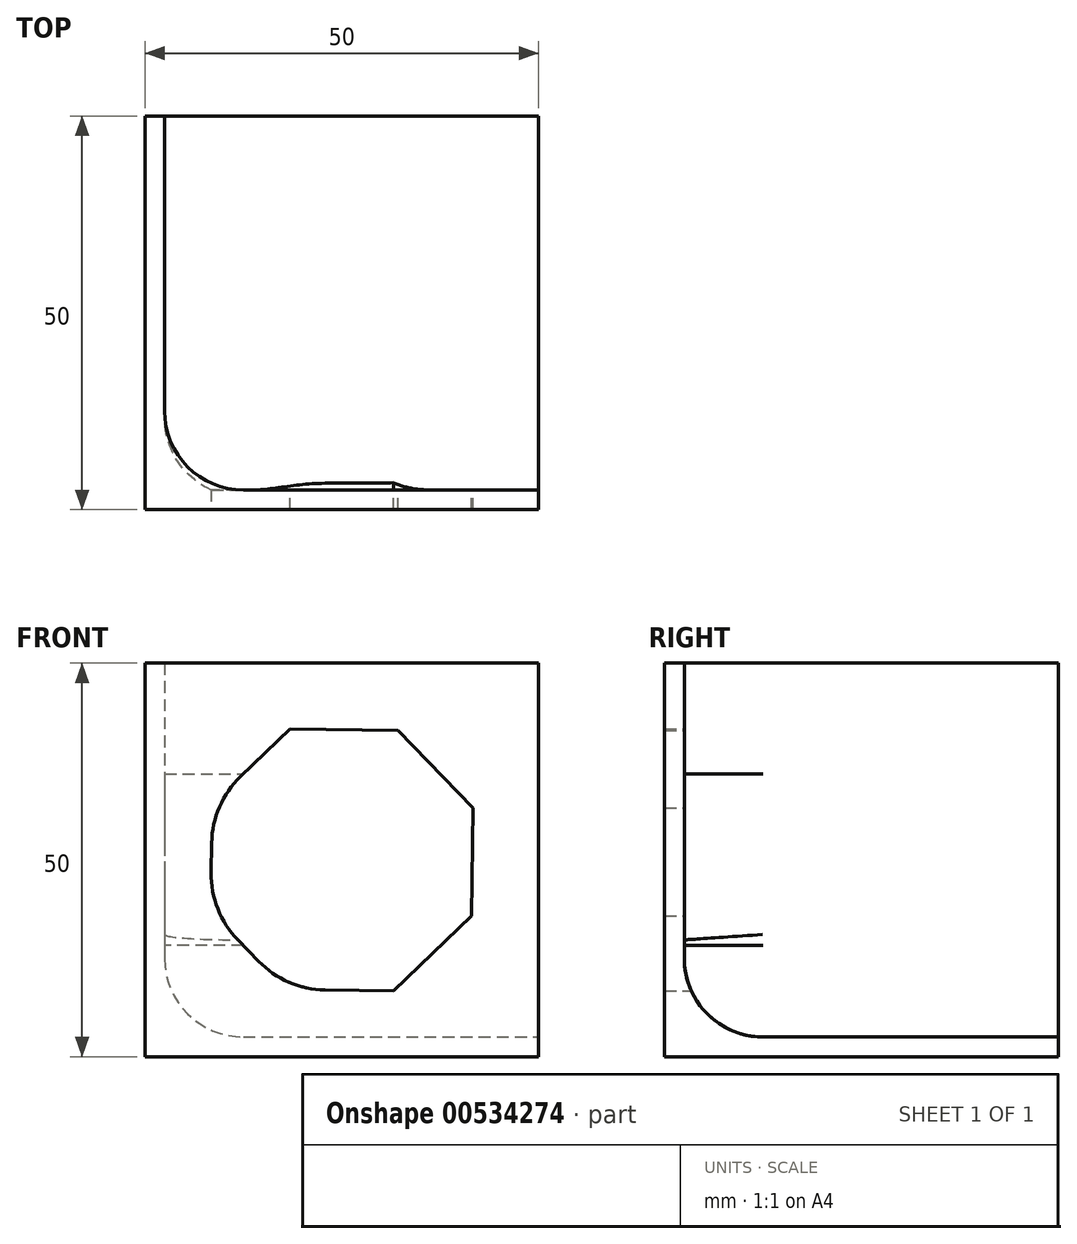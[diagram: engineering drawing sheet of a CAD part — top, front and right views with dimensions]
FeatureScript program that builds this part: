
annotation { "Feature Type Name" : "Feature", "Feature Type Description" : "" }
export const myFeature = defineFeature(function(context is Context, id is Id, definition is map)
    precondition{}
    {
        {
            var Q0;
            Q0=qCreatedBy(makeId("Top.planeOp"),FACE);
            var sketch = newSketch(context, id + "F0", { "sketchPlane" : qUnion([Q0])});
            skLineSegment(sketch, "E0.bottom", {"start": v(-25, -25) * mm, "end": v(25, -25) * mm});
            skLineSegment(sketch, "E0.top", {"start": v(-25, 25) * mm, "end": v(25, 25) * mm});
            skLineSegment(sketch, "E0.left", {"start": v(-25, -25) * mm, "end": v(-25, 25) * mm});
            skLineSegment(sketch, "E0.right", {"start": v(25, -25) * mm, "end": v(25, 25) * mm});
            skLineSegment(sketch, "E1", {"start": v(0, 0) * mm, "end": v(0, 66.24) * mm, "construction": true});
            skSolve(sketch);
        }
        {
            var Q0;
            Q0=makeQuery(id+"F0.imprint","IMPRINT",FACE,{"disambiguationData":[TD([[makeQuery(id+"F0.imprint","IMPRINT",EDGE,{"derivedFrom":sQuery(id+"F0.wireOp",EDGE,"E0.bottom")}),1.0]])]});
            extrude(context, id + "F1", {"entities" : qUnion([Q0]), "depth" : 50 * mm, "offsetDistance" : 25 * mm, "symmetric" : true});
        }
        {
            var Q0;
            Q0=makeQuery(id+"F1.opExtrude","CAP_FACE",FACE,{"disambiguationData":[OSD([sQuery(id+"F0.wireOp",EDGE,"E0.bottom"),sQuery(id+"F0.wireOp",EDGE,"E0.top"),sQuery(id+"F0.wireOp",EDGE,"E0.left"),sQuery(id+"F0.wireOp",EDGE,"E0.right")])],"isStart":false});
            var Q1;
            Q1=makeQuery(id+"F1.opExtrude","SWEPT_FACE",FACE,{"disambiguationData":[OSD([sQuery(id+"F0.wireOp",EDGE,"E0.top")])]});
            var Q2;
            Q2=makeQuery(id+"F1.opExtrude","SWEPT_FACE",FACE,{"disambiguationData":[OSD([sQuery(id+"F0.wireOp",EDGE,"E0.right")])]});
            shell(context, id + "F2", {"entities" : qUnion([Q0, Q1, Q2]), "thickness" : 2.5 * mm});
        }
        {
            var Q0;
            Q0=qCreatedBy(makeId("Front.planeOp"),FACE);
            var sketch = newSketch(context, id + "F3", { "sketchPlane" : qUnion([Q0])});
            skCircle(sketch, "E2.cCircle", {"center": v(0, 0) * mm, "radius": 16.56 * mm, "construction": true});
            skLineSegment(sketch, "E2.0", {"start": v(7.12, 16.45) * mm, "end": v(16.66, 6.6) * mm});
            skLineSegment(sketch, "E2.1", {"start": v(16.66, 6.6) * mm, "end": v(16.45, -7.12) * mm});
            skLineSegment(sketch, "E2.2", {"start": v(16.45, -7.12) * mm, "end": v(6.6, -16.66) * mm});
            skLineSegment(sketch, "E2.3", {"start": v(6.6, -16.66) * mm, "end": v(-7.12, -16.45) * mm});
            skLineSegment(sketch, "E2.4", {"start": v(-7.12, -16.45) * mm, "end": v(-16.66, -6.6) * mm});
            skLineSegment(sketch, "E2.5", {"start": v(-16.66, -6.6) * mm, "end": v(-16.45, 7.12) * mm});
            skLineSegment(sketch, "E2.6", {"start": v(-16.45, 7.12) * mm, "end": v(-6.6, 16.66) * mm});
            skLineSegment(sketch, "E2.7", {"start": v(-6.6, 16.66) * mm, "end": v(7.12, 16.45) * mm});
            skPoint(sketch, "E2.0.midPoint", {"position": v(11.89, 11.52) * mm});
            skSolve(sketch);
        }
        {
            var Q0;
            Q0 = qSketchRegion(id + "F3", true);
            extrude(context, id + "F4", {"entities" : qUnion([Q0]), "operationType" : NewBodyOperationType.REMOVE, "depth" : 70 * mm, "offsetDistance" : 25 * mm});
        }
        {
            var Q0;
            Q0=makeQuery(id+"F4.boolean.opBoolean","COPY",EDGE,{"derivedFrom":makeQuery(id+"F4.opExtrude","SWEPT_EDGE",EDGE,{"disambiguationData":[OSD([sQuery(id+"F3.wireOp",EDGE,"E2.5"),sQuery(id+"F3.wireOp",EDGE,"E2.6")])]})});
            var Q1;
            Q1=makeQuery(id+"F4.boolean.opBoolean","COPY",EDGE,{"derivedFrom":makeQuery(id+"F4.opExtrude","SWEPT_EDGE",EDGE,{"disambiguationData":[OSD([sQuery(id+"F3.wireOp",EDGE,"E2.4"),sQuery(id+"F3.wireOp",EDGE,"E2.5")])]})});
            var Q2;
            Q2=makeQuery(id+"F4.boolean.opBoolean","COPY",EDGE,{"derivedFrom":makeQuery(id+"F4.opExtrude","SWEPT_EDGE",EDGE,{"disambiguationData":[OSD([sQuery(id+"F3.wireOp",EDGE,"E2.3"),sQuery(id+"F3.wireOp",EDGE,"E2.4")])]})});
            fillet(context, id + "F5", {"entities" : qUnion([Q0, Q1, Q2]), "radius" : 12 * mm, "tangentPropagation" : true, "allowEdgeOverflow" : false});
        }
        {
            var Q0;
            Q0=makeQuery(id+"F2.opShell","OFFSET_EDGE",EDGE,{"disambiguationData":[OSD([sQuery(id+"F0.wireOp",EDGE,"E0.bottom"),sQuery(id+"F0.wireOp",EDGE,"E0.left")])]});
            var Q1;
            {var subQ0=sQuery(id+"F0.wireOp",EDGE,"E0.bottom");Q1=makeQuery(id+"F2.opShell","OFFSET_EDGE",EDGE,{"disambiguationData":[OSD([subQ0]),TDD([makeQuery(id+"F1.opExtrude","CAP_EDGE",EDGE,{"disambiguationData":[OSD([subQ0])],"isStart":true})])]});}
            var Q2;
            {var subQ0=sQuery(id+"F0.wireOp",EDGE,"E0.left");Q2=makeQuery(id+"F2.opShell","OFFSET_EDGE",EDGE,{"disambiguationData":[OSD([subQ0]),TDD([makeQuery(id+"F1.opExtrude","CAP_EDGE",EDGE,{"disambiguationData":[OSD([subQ0])],"isStart":true})])]});}
            fillet(context, id + "F6", {"entities" : qUnion([Q0, Q1, Q2]), "radius" : 10 * mm, "tangentPropagation" : true, "allowEdgeOverflow" : false});
        }
    });
